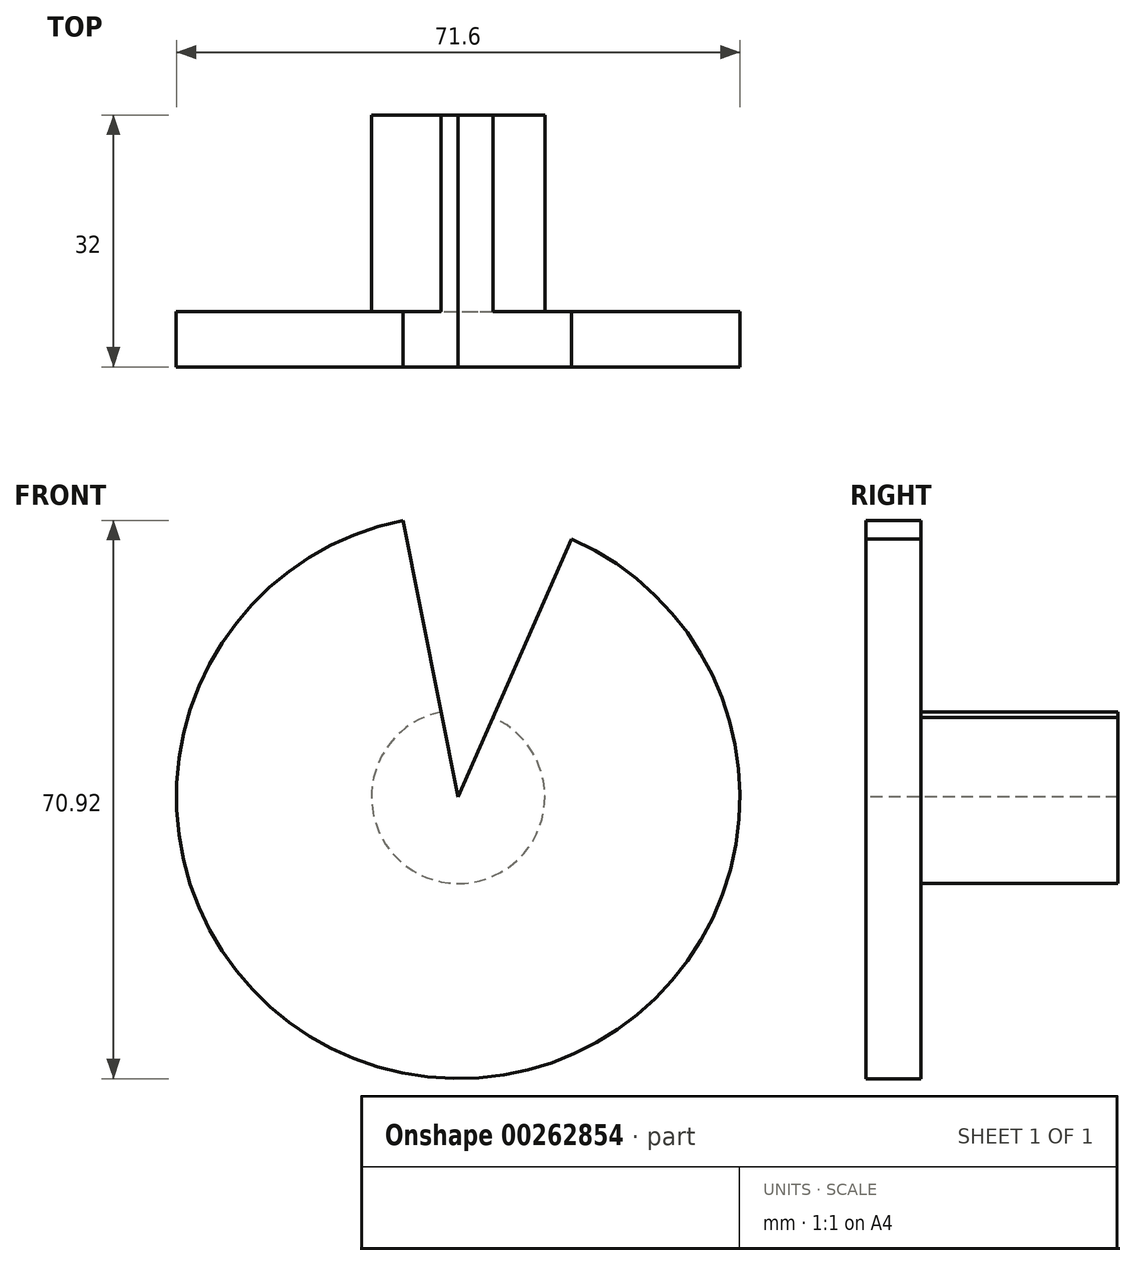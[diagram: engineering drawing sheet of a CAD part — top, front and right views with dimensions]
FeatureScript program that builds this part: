
annotation { "Feature Type Name" : "Feature", "Feature Type Description" : "" }
export const myFeature = defineFeature(function(context is Context, id is Id, definition is map)
    precondition{}
    {
        {
            var Q0;
            Q0=qCreatedBy(makeId("Front.planeOp"),FACE);
            var sketch = newSketch(context, id + "F0", { "sketchPlane" : qUnion([Q0])});
            skCircle(sketch, "E0", {"center": v(-12.78, 38.12) * mm, "radius": 11 * mm});
            skSolve(sketch);
        }
        {
            var Q0;
            Q0 = qSketchRegion(id + "F0", true);
            extrude(context, id + "F1", {"entities" : qUnion([Q0]), "depth" : 25 * mm, "offsetDistance" : 25 * mm});
        }
        {
            var Q0;
            Q0=makeQuery(id+"F1.opExtrude","CAP_FACE",FACE,{"disambiguationData":[OSD([sQuery(id+"F0.wireOp",EDGE,"E0")])],"isStart":false});
            var sketch = newSketch(context, id + "F2", { "sketchPlane" : qUnion([Q0])});
            skCircle(sketch, "E1", {"center": v(-12.78, 38.12) * mm, "radius": 35.8 * mm});
            skSolve(sketch);
        }
        {
            var Q0;
            Q0 = qSketchRegion(id + "F2", true);
            extrude(context, id + "F3", {"entities" : qUnion([Q0]), "operationType" : NewBodyOperationType.ADD, "depth" : 7 * mm, "offsetDistance" : 25 * mm});
        }
        {
            var Q0;
            Q0=makeQuery(id+"F3.opExtrude","CAP_FACE",FACE,{"disambiguationData":[OSD([sQuery(id+"F2.wireOp",EDGE,"E1")])],"isStart":false});
            var sketch = newSketch(context, id + "F4", { "sketchPlane" : qUnion([Q0])});
            skLineSegment(sketch, "E2", {"start": v(-19.78, 73.23) * mm, "end": v(-12.78, 38.12) * mm});
            skLineSegment(sketch, "E3", {"start": v(-12.78, 38.12) * mm, "end": v(1.63, 70.89) * mm});
            skLineSegment(sketch, "E4", {"start": v(1.63, 70.89) * mm, "end": v(-7.42, 82.68) * mm});
            skLineSegment(sketch, "E5", {"start": v(-7.42, 82.68) * mm, "end": v(-19.78, 73.23) * mm});
            skSolve(sketch);
        }
        {
            var Q0;
            Q0 = qSketchRegion(id + "F4", true);
            extrude(context, id + "F5", {"entities" : qUnion([Q0]), "operationType" : NewBodyOperationType.REMOVE, "endBound" : BoundingType.THROUGH_ALL, "oppositeDirection" : true, "depth" : 54.1 * mm, "offsetDistance" : 25 * mm});
        }
    });
